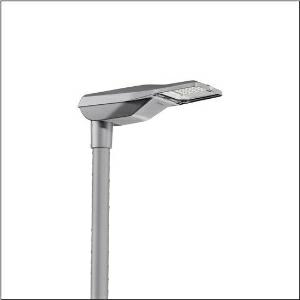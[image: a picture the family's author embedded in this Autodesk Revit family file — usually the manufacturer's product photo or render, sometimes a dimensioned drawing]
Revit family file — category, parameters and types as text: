
# Revit family: streetlight_sl_21_iq_micro___st1_0a_5xe1d61d08cb_4c5c
name_source: partatom
category: Lighting Fixtures
units: mm (PartAtom-declared; Revit-internal decimal feet)

## family parameters
Cut with Voids When Loaded = No
Host = Face
Light Source = No
Part Type = Normal
Room Calculation Point = No
Round Connector Dimension = Use Diameter
Shared = No

## types (1)
- --- (1 x LED, 2570 lm, 19.4 W, 2700K)
    Apparent Load = 19 VA
    CIE Flux Codes = 37 72 97 100 100
    Color Rendering = 70
    Color Temperature = 2700K
    Default Elevation = 1800 mm
    Description = Streetlight SL 21 iQ micro, mast luminaire, primary light control with lens, of PMMA, primary optical cover: cover, of toughened safety glass, transparent, light distribution: ST1.0a, light emission: direct distribution, primary light characteristic: asymmetric, installation type: post-top, side-entry, LED, High Power LED, rated luminous flux: 2.570lm, luminous efficacy: 133lm/W, light colour: 727, colour temperature: 2700K, control gear: iQ-Comfort, control: Auto-Match, Temp-Guard, Lumen-Switch, Night-Set, Smart-Wire, Light-Fading, Desk-Remote (wireless, voltage-free reading and setting of iQ features in the workshop via application-optimized NFC function/RFID function), optimised constant luminous flux control (CLO 2.0), pre-setting: linear dimming characteristic, mains connection: 220..240V, AC, 50/60Hz, start of lifetime: 19W, end of service life: 20W, reduction: 10W, luminaire housing, of diecast aluminium, powder-coated, Siteco® metallic grey (DB 702S), corrosivity category C5 mid according to DIN EN ISO 12944, please order mast flange separately, inclination adjustable: 0°, 5°, 10°, 15°, sealing non-destructively replaceable, multi-level sealing system, length: 528mm, width: 235mm, height: 110mm, mast flange for spigot size: 42mm (side-entry): 5XC10008XM4, 60/48mm (side-entry/post-top): 5XC10108XM2, 76/60mm (side-entry/post-top): 5XC10108XM1, protection rating (complete): IP66, insulation class (complete): insulation class II (safety insulation), certification: CE, ENEC, ENEC+, VDE, impact resistance: IK10, permissible operating ambient temperature for outdoor applications: -40..+50°C, standard-compliant lighting for roads and squares, packaging unit: 1 piece

Light Distribution: ST1.0a
    Height = 110 mm
    Lamp = 1 x LED
    Lamp Light Flux = 2570 lm
    Lamp Power = 19.4 W
    Lamp count = 1
    Length = 528 mm
    Luminous efficacy = 132 lm/W
    Manufacturer = Siteco
    ModVariant = No
    Model = 5XE1D61D08CB
    Number of Poles = 1
    OnlyDefault = Yes
    Power Factor = 1
    Product Name = Streetlight SL 21 iQ micro | ST1.0a
    Product group = mast luminaire | pylon top
    ProductGroupID = 6100
    Protection Class = Protection class II
    Protection Degree = IP 66
    RLX_Detail_Level = 1
    RLX_Emergency_Light_Flux = 0 lm
    RLX_Emergency_Type = 0
    RLX_Emergency_Type_DB = No
    RlxData = <blob elided: 98773 chars, md5=1a854af6>
    Socket = socket
    Standby Power = 0 W
    System Light Flux = 2570 lm
    System Power = 19 W
    Type Comments = factory setting: luminous flux: 100 % | dim-lin: 254 | 387 mA
    Type Image = l_1006881.jpg
    URL = http://relux.com
    VarID = @adj_160623
    Voltage = 0 V
    Weight = 0.00 kg
    Width = 235 mm

## geometry (parser evidence)
native form markers: Blend x4, Sweep x11
no freeform markers — native parametric forms only
